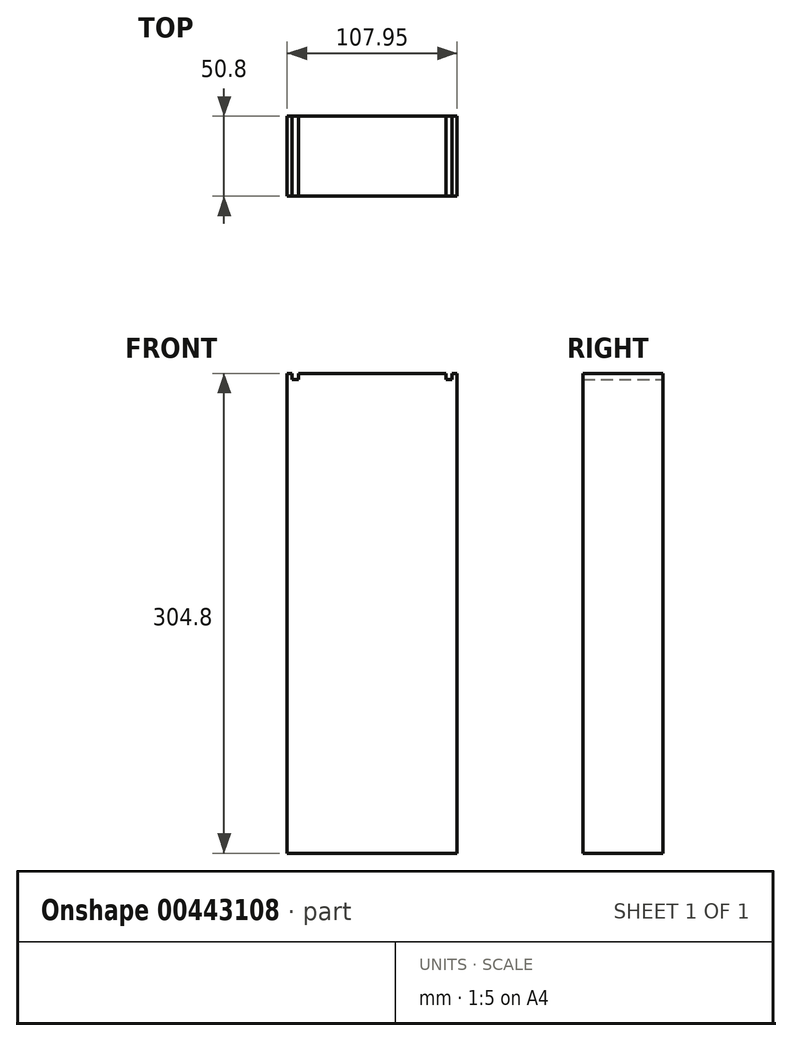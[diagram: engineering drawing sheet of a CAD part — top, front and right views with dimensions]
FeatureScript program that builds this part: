
annotation { "Feature Type Name" : "Feature", "Feature Type Description" : "" }
export const myFeature = defineFeature(function(context is Context, id is Id, definition is map)
    precondition{}
    {
        {
            var Q0;
            Q0=qCreatedBy(makeId("Front.planeOp"),FACE);
            var sketch = newSketch(context, id + "F0", { "sketchPlane" : qUnion([Q0])});
            skLineSegment(sketch, "E0.bottom", {"start": v(-183.37, 241.07) * mm, "end": v(-180.2, 241.07) * mm});
            skLineSegment(sketch, "E0.top", {"start": v(-183.37, -63.73) * mm, "end": v(-75.42, -63.73) * mm});
            skLineSegment(sketch, "E0.left", {"start": v(-183.37, 241.07) * mm, "end": v(-183.37, -63.73) * mm});
            skLineSegment(sketch, "E0.right", {"start": v(-75.42, 241.07) * mm, "end": v(-75.42, -63.73) * mm});
            skLineSegment(sketch, "E1.top", {"start": v(-180.2, 237.07) * mm, "end": v(-176.2, 237.07) * mm});
            skLineSegment(sketch, "E1.left", {"start": v(-180.2, 241.07) * mm, "end": v(-180.2, 237.07) * mm});
            skLineSegment(sketch, "E1.right", {"start": v(-176.2, 241.07) * mm, "end": v(-176.2, 237.07) * mm});
            skLineSegment(sketch, "E2.top", {"start": v(-82.6, 237.07) * mm, "end": v(-78.6, 237.07) * mm});
            skLineSegment(sketch, "E2.left", {"start": v(-82.6, 241.07) * mm, "end": v(-82.6, 237.07) * mm});
            skLineSegment(sketch, "E2.right", {"start": v(-78.6, 241.07) * mm, "end": v(-78.6, 237.07) * mm});
            skLineSegment(sketch, "E3.trimOffspring", {"start": v(-78.6, 241.07) * mm, "end": v(-75.42, 241.07) * mm});
            skLineSegment(sketch, "E4.trimOffspring", {"start": v(-176.2, 241.07) * mm, "end": v(-82.6, 241.07) * mm});
            skSolve(sketch);
        }
        {
            var Q0;
            Q0=makeQuery(id+"F0.imprint","IMPRINT",FACE,{"disambiguationData":[TD([[makeQuery(id+"F0.imprint","IMPRINT",EDGE,{"derivedFrom":sQuery(id+"F0.wireOp",EDGE,"E0.bottom")}),-1.0]])]});
            extrude(context, id + "F1", {"entities" : qUnion([Q0]), "depth" : 50.8 * mm});
        }
    });
